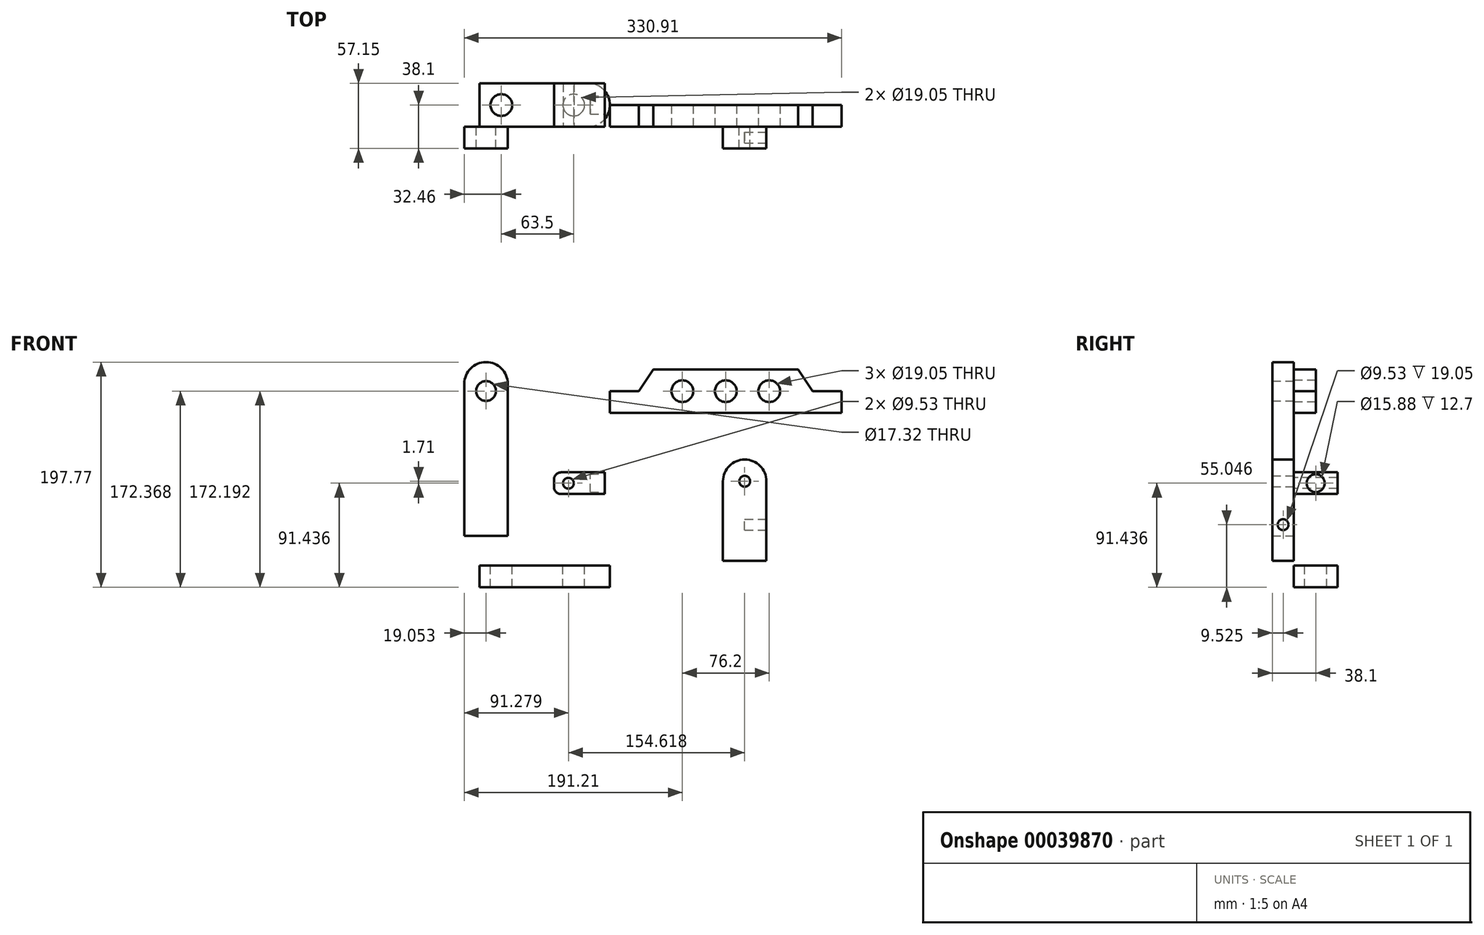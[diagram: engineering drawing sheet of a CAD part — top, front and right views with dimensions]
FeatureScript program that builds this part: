
annotation { "Feature Type Name" : "Feature", "Feature Type Description" : "" }
export const myFeature = defineFeature(function(context is Context, id is Id, definition is map)
    precondition{}
    {
        {
            var Q0;
            Q0=qCreatedBy(makeId("Front.planeOp"),FACE);
            var sketch = newSketch(context, id + "F0", { "sketchPlane" : qUnion([Q0])});
            skLineSegment(sketch, "E0.bottom", {"start": v(-49.13, 22.21) * mm, "end": v(-4.68, 22.21) * mm});
            skLineSegment(sketch, "E0.top", {"start": v(-49.13, 41.26) * mm, "end": v(-4.68, 41.26) * mm});
            skLineSegment(sketch, "E0.left", {"start": v(-49.13, 22.21) * mm, "end": v(-49.13, 41.26) * mm});
            skLineSegment(sketch, "E0.right", {"start": v(-4.68, 22.21) * mm, "end": v(-4.68, 41.26) * mm});
            skSolve(sketch);
        }
        {
            var Q0;
            Q0 = qSketchRegion(id + "F0", true);
            extrude(context, id + "F1", {"entities" : qUnion([Q0]), "oppositeDirection" : true, "depth" : 38.1 * mm});
        }
        {
            var Q0;
            Q0=makeQuery(id+"F1.opExtrude","CAP_FACE",FACE,{"disambiguationData":[OSD([sQuery(id+"F0.wireOp",EDGE,"E0.bottom"),sQuery(id+"F0.wireOp",EDGE,"E0.top"),sQuery(id+"F0.wireOp",EDGE,"E0.left"),sQuery(id+"F0.wireOp",EDGE,"E0.right")])],"isStart":true});
            var sketch = newSketch(context, id + "F2", { "sketchPlane" : qUnion([Q0])});
            skLineSegment(sketch, "E1", {"start": v(-49.13, 31.74) * mm, "end": v(-4.68, 31.74) * mm});
            skCircle(sketch, "E2", {"center": v(-36.43, 31.74) * mm, "radius": 4.76 * mm});
            skSolve(sketch);
        }
        {
            var Q0;
            Q0 = qSketchRegion(id + "F2", true);
            extrude(context, id + "F3", {"entities" : qUnion([Q0]), "operationType" : NewBodyOperationType.REMOVE, "oppositeDirection" : true, "depth" : 43.18 * mm});
        }
        {
            var Q0;
            Q0=makeQuery(id+"F1.opExtrude","SWEPT_FACE",FACE,{"disambiguationData":[OSD([sQuery(id+"F0.wireOp",EDGE,"E0.right")])]});
            var sketch = newSketch(context, id + "F4", { "sketchPlane" : qUnion([Q0])});
            skCircle(sketch, "E3", {"center": v(19.05, 31.74) * mm, "radius": 7.94 * mm});
            skPoint(sketch, "E3.centerSnap0", {"position": v(0, 31.74) * mm});
            skSolve(sketch);
        }
        {
            var Q0;
            Q0=makeQuery(id+"F4.imprint","IMPRINT",FACE,{"disambiguationData":[TD([[makeQuery(id+"F4.imprint","IMPRINT",EDGE,{"derivedFrom":sQuery(id+"F4.wireOp",EDGE,"E3")}),1.0]])]});
            extrude(context, id + "F5", {"entities" : qUnion([Q0]), "operationType" : NewBodyOperationType.REMOVE, "oppositeDirection" : true, "depth" : 12.7 * mm});
        }
        {
            var Q0;
            Q0=makeQuery(id+"F1.opExtrude","SWEPT_EDGE",EDGE,{"disambiguationData":[OSD([sQuery(id+"F0.wireOp",EDGE,"E0.top"),sQuery(id+"F0.wireOp",EDGE,"E0.left")])]});
            var Q1;
            Q1=makeQuery(id+"F1.opExtrude","SWEPT_EDGE",EDGE,{"disambiguationData":[OSD([sQuery(id+"F0.wireOp",EDGE,"E0.bottom"),sQuery(id+"F0.wireOp",EDGE,"E0.left")])]});
            fillet(context, id + "F6", {"entities" : qUnion([Q0, Q1]), "radius" : 6.35 * mm, "tangentPropagation" : true, "allowEdgeOverflow" : false});
        }
        {
            var Q0;
            Q0=qCreatedBy(makeId("Front.planeOp"),FACE);
            var sketch = newSketch(context, id + "F7", { "sketchPlane" : qUnion([Q0])});
            skLineSegment(sketch, "E4.bottom", {"start": v(99.14, 52.5) * mm, "end": v(137.24, 52.5) * mm});
            skLineSegment(sketch, "E4.top", {"start": v(99.14, -36.4) * mm, "end": v(137.24, -36.4) * mm});
            skLineSegment(sketch, "E4.left", {"start": v(99.14, 52.5) * mm, "end": v(99.14, -36.4) * mm});
            skLineSegment(sketch, "E4.right", {"start": v(137.24, 52.5) * mm, "end": v(137.24, -36.4) * mm});
            skCircle(sketch, "E5", {"center": v(118.19, 33.45) * mm, "radius": 4.76 * mm});
            skSolve(sketch);
        }
        {
            var Q0;
            Q0 = qSketchRegion(id + "F7", true);
            extrude(context, id + "F8", {"entities" : qUnion([Q0]), "depth" : 19.05 * mm});
        }
        {
            var Q0;
            Q0=makeQuery(id+"F8.opExtrude","SWEPT_FACE",FACE,{"disambiguationData":[OSD([sQuery(id+"F7.wireOp",EDGE,"E4.right")])]});
            var sketch = newSketch(context, id + "F9", { "sketchPlane" : qUnion([Q0])});
            skCircle(sketch, "E6", {"center": v(-9.53, -4.65) * mm, "radius": 4.76 * mm});
            skPoint(sketch, "E6.centerSnap0", {"position": v(-9.53, -36.4) * mm});
            skSolve(sketch);
        }
        {
            var Q0;
            Q0 = qSketchRegion(id + "F9", true);
            extrude(context, id + "F10", {"entities" : qUnion([Q0]), "operationType" : NewBodyOperationType.REMOVE, "oppositeDirection" : true, "depth" : 19.05 * mm});
        }
        {
            var Q0;
            Q0=makeQuery(id+"F8.opExtrude","SWEPT_EDGE",EDGE,{"disambiguationData":[OSD([sQuery(id+"F7.wireOp",EDGE,"E4.bottom"),sQuery(id+"F7.wireOp",EDGE,"E4.right")])]});
            var Q1;
            Q1=makeQuery(id+"F8.opExtrude","SWEPT_EDGE",EDGE,{"disambiguationData":[OSD([sQuery(id+"F7.wireOp",EDGE,"E4.bottom"),sQuery(id+"F7.wireOp",EDGE,"E4.left")])]});
            fillet(context, id + "F11", {"entities" : qUnion([Q0, Q1]), "radius" : 19.05 * mm, "tangentPropagation" : true, "allowEdgeOverflow" : false});
        }
        {
            var Q0;
            Q0=qCreatedBy(makeId("Front.planeOp"),FACE);
            var sketch = newSketch(context, id + "F12", { "sketchPlane" : qUnion([Q0])});
            skLineSegment(sketch, "E7.bottom", {"start": v(-114.3, -40.65) * mm, "end": v(0, -40.65) * mm});
            skLineSegment(sketch, "E7.top", {"start": v(-114.3, -59.7) * mm, "end": v(0, -59.7) * mm});
            skLineSegment(sketch, "E7.left", {"start": v(-114.3, -40.65) * mm, "end": v(-114.3, -59.7) * mm});
            skLineSegment(sketch, "E7.right", {"start": v(0, -40.65) * mm, "end": v(0, -59.7) * mm});
            skSolve(sketch);
        }
        {
            var Q0;
            Q0 = qSketchRegion(id + "F12", true);
            extrude(context, id + "F13", {"entities" : qUnion([Q0]), "oppositeDirection" : true, "depth" : 38.1 * mm});
        }
        {
            var Q0;
            Q0=makeQuery(id+"F13.opExtrude","SWEPT_FACE",FACE,{"disambiguationData":[OSD([sQuery(id+"F12.wireOp",EDGE,"E7.bottom")])]});
            var sketch = newSketch(context, id + "F14", { "sketchPlane" : qUnion([Q0])});
            skCircle(sketch, "E8", {"center": v(-95.25, 19.05) * mm, "radius": 9.53 * mm});
            skPoint(sketch, "E8.centerSnap0", {"position": v(-114.3, 19.05) * mm});
            skCircle(sketch, "E9", {"center": v(-31.75, 19.05) * mm, "radius": 9.53 * mm});
            skPoint(sketch, "E9.centerSnap0", {"position": v(0, 19.05) * mm});
            skSolve(sketch);
        }
        {
            var Q0;
            Q0 = qSketchRegion(id + "F14", true);
            extrude(context, id + "F15", {"entities" : qUnion([Q0]), "operationType" : NewBodyOperationType.REMOVE, "oppositeDirection" : true, "depth" : 101.6 * mm});
        }
        {
            var Q0;
            Q0=makeQuery(id+"F13.opExtrude","CAP_EDGE",EDGE,{"disambiguationData":[OSD([sQuery(id+"F12.wireOp",EDGE,"E7.right")])],"isStart":false});
            var Q1;
            Q1=makeQuery(id+"F13.opExtrude","CAP_EDGE",EDGE,{"disambiguationData":[OSD([sQuery(id+"F12.wireOp",EDGE,"E7.right")])],"isStart":true});
            fillet(context, id + "F16", {"entities" : qUnion([Q0, Q1]), "radius" : 19.05 * mm, "tangentPropagation" : true, "allowEdgeOverflow" : false});
        }
        {
            var Q0;
            Q0=qCreatedBy(makeId("Front.planeOp"),FACE);
            var sketch = newSketch(context, id + "F17", { "sketchPlane" : qUnion([Q0])});
            skLineSegment(sketch, "E10.bottom", {"start": v(-108.66, 138.07) * mm, "end": v(-108.66, 138.07) * mm});
            skLineSegment(sketch, "E10.top", {"start": v(-127.7, -14.33) * mm, "end": v(-89.6, -14.33) * mm});
            skLineSegment(sketch, "E10.left", {"start": v(-127.7, 119.02) * mm, "end": v(-127.7, -14.33) * mm});
            skLineSegment(sketch, "E10.right", {"start": v(-89.6, 119.02) * mm, "end": v(-89.6, -14.33) * mm});
            skCircle(sketch, "E11", {"center": v(-108.66, 112.67) * mm, "radius": 8.66 * mm});
            skPoint(sketch, "E12.visualSharp", {"position": v(-127.7, 138.07) * mm});
            skArc(sketch, "E12.filletArc", {"start": v(-108.66, 138.07) * mm, "mid": v(-122.13, 132.49) * mm, "end": v(-127.7, 119.02) * mm});
            skPoint(sketch, "E13.visualSharp", {"position": v(-89.6, 138.07) * mm});
            skArc(sketch, "E13.filletArc", {"start": v(-89.6, 119.02) * mm, "mid": v(-95.19, 132.49) * mm, "end": v(-108.66, 138.07) * mm});
            skSolve(sketch);
        }
        {
            var Q0;
            Q0 = qSketchRegion(id + "F17", true);
            extrude(context, id + "F18", {"entities" : qUnion([Q0]), "depth" : 19.05 * mm});
        }
        {
            var Q0;
            Q0=qCreatedBy(makeId("Front.planeOp"),FACE);
            var sketch = newSketch(context, id + "F19", { "sketchPlane" : qUnion([Q0])});
            skLineSegment(sketch, "E14.bottom", {"start": v(38.1, 131.54) * mm, "end": v(165.1, 131.54) * mm});
            skLineSegment(sketch, "E14.top", {"start": v(0, 93.44) * mm, "end": v(203.2, 93.44) * mm});
            skLineSegment(sketch, "E14.left", {"start": v(0, 112.5) * mm, "end": v(0, 93.44) * mm});
            skLineSegment(sketch, "E14.right", {"start": v(203.2, 112.5) * mm, "end": v(203.2, 93.44) * mm});
            skLineSegment(sketch, "E15", {"start": v(101.6, 131.54) * mm, "end": v(101.6, 93.44) * mm});
            skLineSegment(sketch, "E16", {"start": v(0, 112.5) * mm, "end": v(101.6, 112.5) * mm});
            skCircle(sketch, "E17", {"center": v(101.6, 112.5) * mm, "radius": 9.53 * mm});
            skCircle(sketch, "E18", {"center": v(63.5, 112.5) * mm, "radius": 9.53 * mm});
            skLineSegment(sketch, "E19", {"start": v(25.4, 112.5) * mm, "end": v(38.1, 131.54) * mm});
            skLineSegment(sketch, "E20.MirrorCS", {"start": v(203.2, 112.5) * mm, "end": v(101.6, 112.5) * mm});
            skLineSegment(sketch, "E21.MirrorCS", {"start": v(177.8, 112.5) * mm, "end": v(165.1, 131.54) * mm});
            skCircle(sketch, "E22.MirrorC", {"center": v(139.7, 112.5) * mm, "radius": 9.53 * mm});
            skPoint(sketch, "E23.orphan", {"position": v(0, 131.54) * mm});
            skPoint(sketch, "E24.orphan", {"position": v(203.2, 131.54) * mm});
            skSolve(sketch);
        }
        {
            var Q0;
            Q0 = qSketchRegion(id + "F19", true);
            extrude(context, id + "F20", {"entities" : qUnion([Q0]), "oppositeDirection" : true, "depth" : 19.05 * mm});
        }
    });
